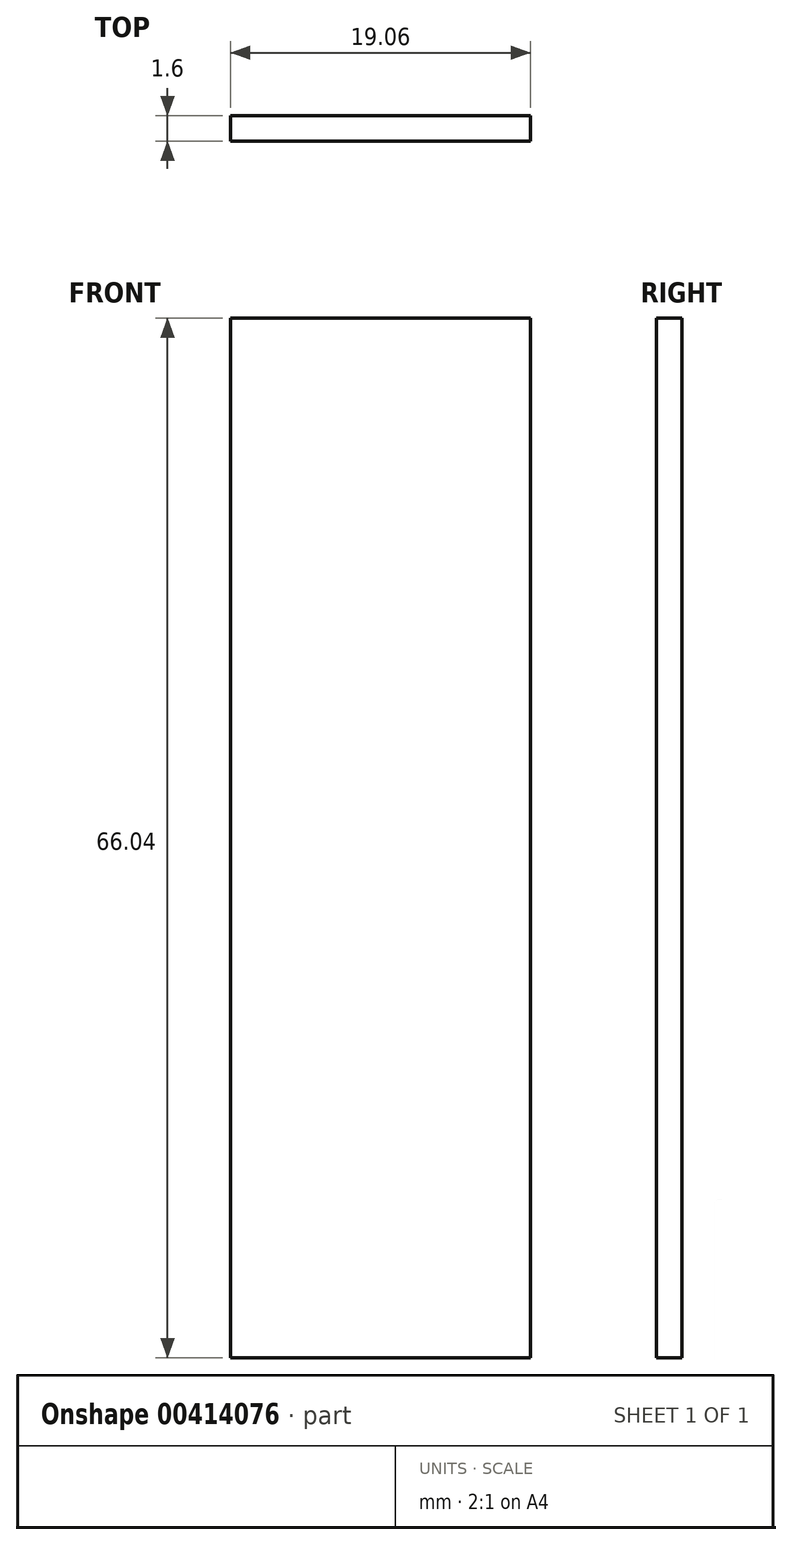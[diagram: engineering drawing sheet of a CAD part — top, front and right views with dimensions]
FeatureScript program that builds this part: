
annotation { "Feature Type Name" : "Feature", "Feature Type Description" : "" }
export const myFeature = defineFeature(function(context is Context, id is Id, definition is map)
    precondition{}
    {
        {
            var Q0;
            Q0=qCreatedBy(makeId("Front.planeOp"),FACE);
            var sketch = newSketch(context, id + "F0", { "sketchPlane" : qUnion([Q0])});
            skLineSegment(sketch, "E0.bottom", {"start": v(8.98, 0) * mm, "end": v(28.03, 0) * mm});
            skLineSegment(sketch, "E0.top", {"start": v(8.97, 66.04) * mm, "end": v(28.02, 66.04) * mm});
            skLineSegment(sketch, "E1.bottom", {"start": v(18.5, 0) * mm, "end": v(8.98, 0) * mm});
            skPoint(sketch, "E1.middle", {"position": v(18.5, 6.35) * mm});
            skLineSegment(sketch, "E2.bottom", {"start": v(28.02, 66.04) * mm, "end": v(8.97, 66.04) * mm});
            skLineSegment(sketch, "E2.top", {"start": v(28.03, 0) * mm, "end": v(8.98, 0) * mm});
            skLineSegment(sketch, "E2.left", {"start": v(28.02, 66.04) * mm, "end": v(28.03, 0) * mm});
            skLineSegment(sketch, "E2.right", {"start": v(8.97, 66.04) * mm, "end": v(8.98, 0) * mm});
            skPoint(sketch, "E2.middle", {"position": v(18.5, 33.02) * mm});
            skPoint(sketch, "E3.orphan", {"position": v(0, 66.04) * mm});
            skPoint(sketch, "E4.orphan", {"position": v(0, 12.7) * mm});
            skPoint(sketch, "E5.orphan", {"position": v(0, 0) * mm});
            skPoint(sketch, "E0.right.end.orphan", {"position": v(37, 12.7) * mm});
            skPoint(sketch, "E6.orphan", {"position": v(37, 0) * mm});
            skPoint(sketch, "E7.orphan", {"position": v(37, 66.04) * mm});
            skPoint(sketch, "E8.start.orphan", {"position": v(18.5, 66.04) * mm});
            skSolve(sketch);
        }
        {
            var Q0;
            {var subQ5=sQuery(id+"F0.wireOp",EDGE,"E2.left");Q0=makeQuery(id+"F0.imprint","IMPRINT",FACE,{"disambiguationData":[TD([[makeQuery(id+"F0.imprint","IMPRINT",EDGE,{"derivedFrom":subQ5}),-1.0]])]});}
            var Q1;
            {var subQ5=sQuery(id+"F0.wireOp",EDGE,"E2.right");Q1=makeQuery(id+"F0.imprint","IMPRINT",FACE,{"disambiguationData":[TD([[makeQuery(id+"F0.imprint","IMPRINT",EDGE,{"derivedFrom":subQ5}),1.0]])]});}
            var Q2;
            {var subQ5=sQuery(id+"F0.wireOp",EDGE,"At2gNgIy-eawO-amjd-7S2Z-JZZ8zG7KdlZu");Q2=makeQuery(id+"F0.imprint","IMPRINT",FACE,{"disambiguationData":[TD([[makeQuery(id+"F0.imprint","IMPRINT",EDGE,{"derivedFrom":subQ5}),1.0]])]});}
            var Q3;
            {var subQ5=sQuery(id+"F0.wireOp",EDGE,"vpTQC8qf-tNg7-m4cR-fTOo-wbTdRuqcnhRd");Q3=makeQuery(id+"F0.imprint","IMPRINT",FACE,{"disambiguationData":[TD([[makeQuery(id+"F0.imprint","IMPRINT",EDGE,{"derivedFrom":subQ5}),-1.0]])]});}
            var Q4;
            {var subQ5=sQuery(id+"F0.wireOp",EDGE,"E1.left");Q4=makeQuery(id+"F0.imprint","IMPRINT",FACE,{"disambiguationData":[TD([[makeQuery(id+"F0.imprint","IMPRINT",EDGE,{"derivedFrom":subQ5}),1.0]])]});}
            var Q5;
            {var subQ5=sQuery(id+"F0.wireOp",EDGE,"E1.right");Q5=makeQuery(id+"F0.imprint","IMPRINT",FACE,{"disambiguationData":[TD([[makeQuery(id+"F0.imprint","IMPRINT",EDGE,{"derivedFrom":subQ5}),-1.0]])]});}
            extrude(context, id + "F1", {"entities" : qUnion([Q0, Q1, Q2, Q3, Q4, Q5]), "depth" : 1.6 * mm});
        }
    });
